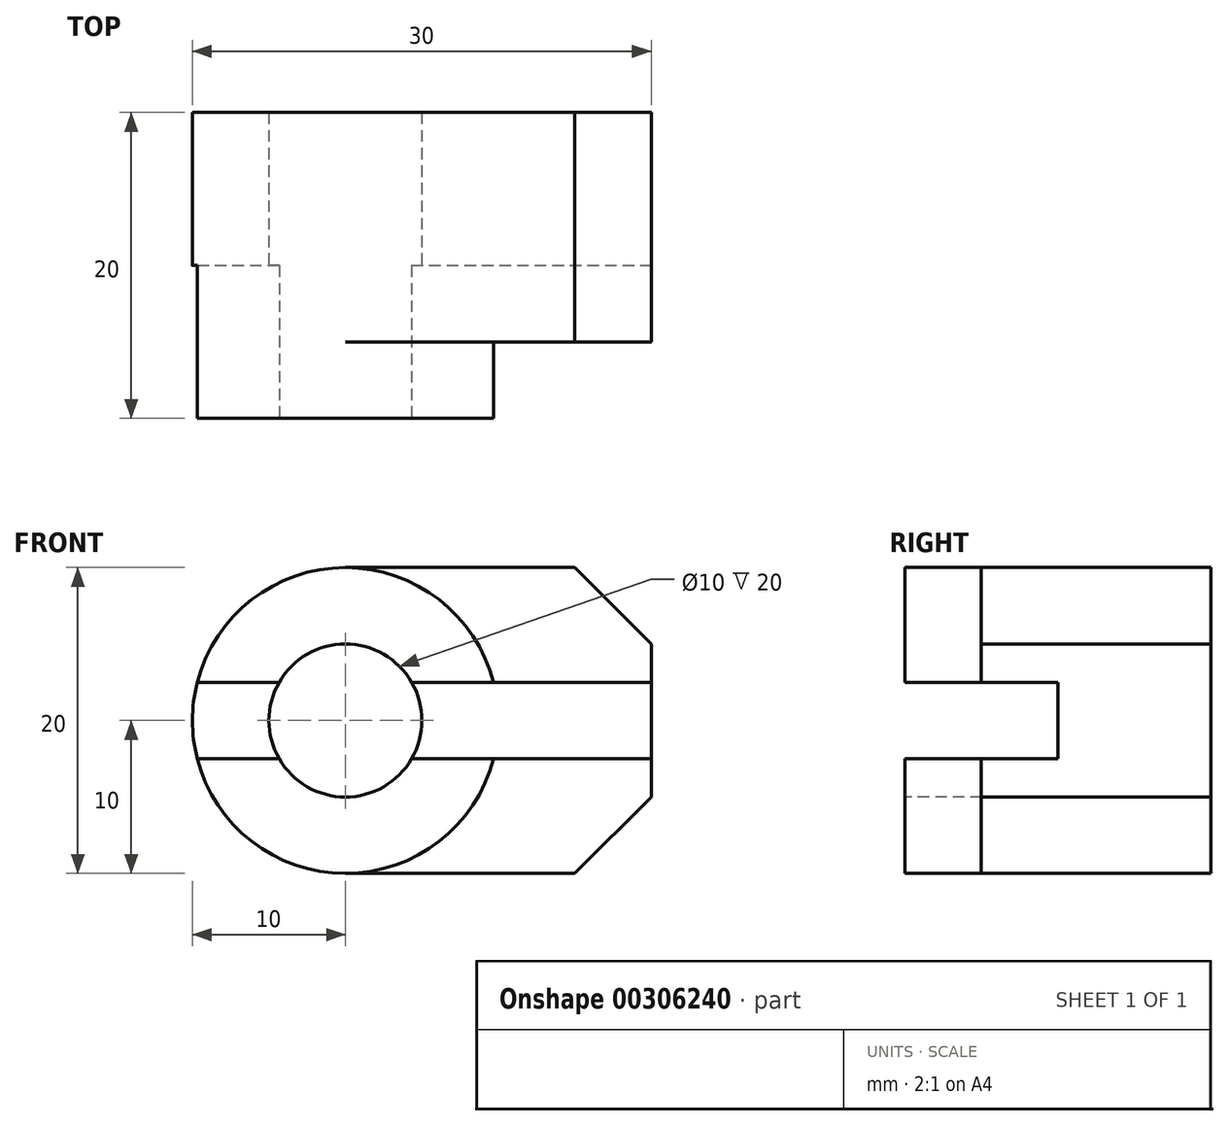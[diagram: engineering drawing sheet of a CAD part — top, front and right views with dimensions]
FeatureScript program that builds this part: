
annotation { "Feature Type Name" : "Feature", "Feature Type Description" : "" }
export const myFeature = defineFeature(function(context is Context, id is Id, definition is map)
    precondition{}
    {
        {
            var Q0;
            Q0=qCreatedBy(makeId("Front.planeOp"),FACE);
            var sketch = newSketch(context, id + "F0", { "sketchPlane" : qUnion([Q0])});
            skCircle(sketch, "E0", {"center": v(0, 0) * mm, "radius": 10 * mm});
            skSolve(sketch);
        }
        {
            var Q0;
            Q0 = qSketchRegion(id + "F0", true);
            extrude(context, id + "F1", {"entities" : qUnion([Q0]), "oppositeDirection" : true, "depth" : 20 * mm});
        }
        {
            var Q0;
            Q0=qCreatedBy(makeId("Front.planeOp"),FACE);
            var sketch = newSketch(context, id + "F2", { "sketchPlane" : qUnion([Q0])});
            skCircle(sketch, "E1", {"center": v(0, 0) * mm, "radius": 5 * mm});
            skSolve(sketch);
        }
        {
            var Q0;
            Q0 = qSketchRegion(id + "F2", true);
            extrude(context, id + "F3", {"entities" : qUnion([Q0]), "operationType" : NewBodyOperationType.REMOVE, "endBound" : BoundingType.THROUGH_ALL, "oppositeDirection" : true, "depth" : 10 * mm});
        }
        {
            var Q0;
            Q0=qCreatedBy(makeId("Front.planeOp"),FACE);
            var sketch = newSketch(context, id + "F4", { "sketchPlane" : qUnion([Q0])});
            skArc(sketch, "E2", {"start": v(0, -10) * mm, "mid": v(10, 0) * mm, "end": v(0, 10) * mm});
            skLineSegment(sketch, "E3", {"start": v(15, 10) * mm, "end": v(20, 5) * mm});
            skLineSegment(sketch, "E4", {"start": v(20, 5) * mm, "end": v(20, -5) * mm});
            skLineSegment(sketch, "E5", {"start": v(20, -5) * mm, "end": v(15, -10) * mm});
            skLineSegment(sketch, "E6", {"start": v(15, -10) * mm, "end": v(0, -10) * mm});
            skLineSegment(sketch, "E7", {"start": v(0, 10) * mm, "end": v(15, 10) * mm});
            skSolve(sketch);
        }
        {
            var Q0;
            Q0 = qSketchRegion(id + "F4", true);
            extrude(context, id + "F5", {"entities" : qUnion([Q0]), "operationType" : NewBodyOperationType.ADD, "oppositeDirection" : true, "depth" : 20 * mm, "hasSecondDirection" : true, "secondDirectionOppositeDirection" : true, "secondDirectionDepth" : 5 * mm});
        }
        {
            var Q0;
            Q0=qCreatedBy(makeId("Right.planeOp"),FACE);
            var sketch = newSketch(context, id + "F6", { "sketchPlane" : qUnion([Q0])});
            skLineSegment(sketch, "E8.bottom", {"start": v(0, 2.5) * mm, "end": v(10, 2.5) * mm});
            skLineSegment(sketch, "E8.top", {"start": v(0, -2.5) * mm, "end": v(10, -2.5) * mm});
            skLineSegment(sketch, "E8.left", {"start": v(0, 2.5) * mm, "end": v(0, -2.5) * mm});
            skLineSegment(sketch, "E8.right", {"start": v(10, 2.5) * mm, "end": v(10, -2.5) * mm});
            skSolve(sketch);
        }
        {
            var Q0;
            Q0 = qSketchRegion(id + "F6", true);
            extrude(context, id + "F7", {"entities" : qUnion([Q0]), "operationType" : NewBodyOperationType.REMOVE, "endBound" : BoundingType.THROUGH_ALL, "oppositeDirection" : true, "depth" : 25 * mm, "hasSecondDirection" : true, "secondDirectionBound" : SecondDirectionBoundingType.THROUGH_ALL, "secondDirectionOppositeDirection" : false, "secondDirectionDepth" : 25 * mm});
        }
    });
